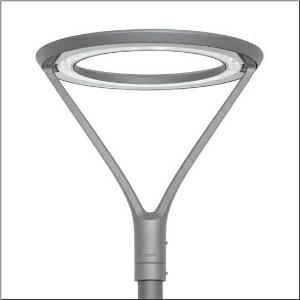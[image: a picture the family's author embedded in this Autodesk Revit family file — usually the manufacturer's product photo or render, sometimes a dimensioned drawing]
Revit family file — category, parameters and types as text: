
# Revit family: dl_r__20___pl1_2s_5xa51283ns008p_0781
name_source: partatom
category: Lighting Fixtures
units: mm (PartAtom-declared; Revit-internal decimal feet)

## family parameters
Cut with Voids When Loaded = No
Host = Face
Light Source = No
Part Type = Normal
Room Calculation Point = No
Round Connector Dimension = Use Diameter
Shared = No

## types (1)
- --- (1 x LED, 5400 lm, 41.9 W, 4000K)
    Apparent Load = 42 VA
    CIE Flux Codes = 33 78 99 100 100
    Color Rendering = 70
    Color Temperature = 4000K
    Default Elevation = 1800 mm
    Description = DL® 20, mast luminaire, primary light control with reflector, highly specular, primary optical cover: cover, of toughened safety glass of clear glass with excellent transmission level, light distribution: PL1.2s, light emission: direct distribution, primary light characteristic: symmetric, installation type: post-top, LED, High Power LED, rated luminous flux: 5.340lm, luminous efficacy: 101lm/W, light colour: 740, colour temperature: 4000K, control gear: Plus, control: overheat protection, power reduction, digital communication interface, constant luminous flux control, time-dependent luminous flux control, flexible luminous flux parameterisation, electronic power reduction, mains connection: 230..240V, 50/60Hz, connection cable pre-assembled, cable length: 5m, start of lifetime: 53W, end of service life: 54W, reduction: 24W, luminaire housing, upper part, of cast aluminium, powder-coated, Siteco® metallic grey (DB 702S), diameter: 690mm, height: 690mm, spigot size: 76mm (post-top), mounting height: 4..6m, luminaire housing, of cast aluminium, powder-coated, Siteco® metallic grey (DB 702S), equipment: Power, protection rating (complete): IP66, insulation class (complete): insulation class II (safety insulation), certification: CE, ENEC, VDE, impact resistance: IK08, permissible operating ambient temperature: -25..+30°C, standard-compliant lighting for roads and squares, packaging unit: 1 piece

Light Distribution: PL1.2s
    Height = 690 mm
    Lamp = 1 x LED
    Lamp Light Flux = 5400 lm
    Lamp Power = 41.9 W
    Lamp count = 1
    Length = 690 mm
    Luminous efficacy = 129 lm/W
    Manufacturer = Siteco
    ModVariant = No
    Model = 5XA51283NS008P
    Number of Poles = 1
    OnlyDefault = Yes
    Power Factor = 1
    Product Name = DL® 20 | PL1.2s
    Product group = mast luminaire | pylon top
    ProductGroupID = 6100
    Protection Class = Protection class II
    Protection Degree = IP 66
    RLX_Detail_Level = 1
    RLX_Emergency_Light_Flux = 0 lm
    RLX_Emergency_Type = 0
    RLX_Emergency_Type_DB = No
    RlxData = <blob elided: 204905 chars, md5=5e13b50e>
    Socket = socket
    Standby Power = 0 W
    System Light Flux = 5400 lm
    System Power = 42 W
    Type Comments = factory setting: luminous flux: 100 % | dim-lin: 254 | 565 mA
    Type Image = l_1006001.jpg
    URL = http://relux.com
    VarID = @adj_076864
    Voltage = 0 V
    Weight = 0.00 kg
    Width = 0 mm  [stored 0 ft]

note: [stored X ft] marks values corroborated as IEEE doubles in the binary element streams (Revit-internal decimal feet)

## geometry (parser evidence)
native form markers: Blend x4, Sweep x10
no freeform markers — native parametric forms only
